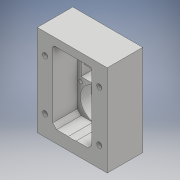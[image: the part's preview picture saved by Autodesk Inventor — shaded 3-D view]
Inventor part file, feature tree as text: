
AUTODESK INVENTOR PART (.ipt)
format: ipt  version: 2018 (Build 220112000, 112)  size: 443,392 bytes
history: native  units: mm
features: sketch x22, projected_geometry x19, extrude x18, hole x4, fillet x3, chamfer x1, mirror x1
ambient origin geometry x8: Origin, YZ Plane, XZ Plane, XY Plane, X Axis, Y Axis, Z Axis, Center Point
bodies: Solid1 (feature_tree)
feature tree (68):
  extrude  "Extrusion1"  Depth=45.0mm
  extrude  "Extrusion2"  Depth=1.95mm
  hole  "Hole1"  [1 undecoded]
  hole  "Hole2"  [1 undecoded]
  fillet  "Fillet1"  Radius=14.0mm
  extrude  "Extrusion3"  Depth=18.5mm
  extrude  "Extrusion4"  Depth=10.0mm
  extrude  "Extrusion5"  Depth=2.195mm
  extrude  "Extrusion6"  Depth=20.5mm
  hole  "Hole3"  [1 undecoded]
  extrude  "Extrusion7"  Depth=0.5mm
  extrude  "Extrusion8"  Depth=5.0mm TaperAngle=0.0deg
  extrude  "Extrusion9"  Depth=10.0mm
  extrude  "Extrusion10"  Depth=10.0mm
  extrude  "Extrusion11"  Depth=14.5mm
  extrude  "Extrusion12"  Depth=20.0mm
  extrude  "Extrusion13"  Depth=5.0mm
  extrude  "Extrusion14"  Depth=5.0mm
  extrude  "Extrusion15"  Depth=5.0mm
  extrude  "Extrusion16"  Depth=5.0mm
  extrude  "Extrusion17"  Depth=5.0mm
  chamfer  "Chamfer1"  Distance=1.0mm
  fillet  "Fillet7"  Radius=20.7mm
  fillet  "Fillet8"  Radius=32.0mm
  mirror  "Mirror1"
  extrude  "Extrusion18"  Depth=5.0mm TaperAngle=0.0deg
  hole  "Hole5"  [1 undecoded]
  sketch  "Sketch1"  dims[d0=24.5mm d1=45.0mm]
  sketch  "Sketch2"  dims[d2=1.95mm d3=0.0mm d4=2.25mm]
  projected_geometry  "Projected Loop1"
  sketch  "Sketch3"  dims[d5=20.0mm d6=2.25mm]
  projected_geometry  "Projected Loop2"
  sketch  "Sketch4"  dims[d7=5.25mm d8=5.25mm d9=14.0mm]
  projected_geometry  "Projected Loop3"
  sketch  "Sketch5"  dims[d10=5.25mm d11=18.5mm]
  projected_geometry  "Projected Loop4"
  sketch  "Sketch6"  dims[d12=10.0mm d13=0.0mm d14=20.5mm]
  projected_geometry  "Projected Loop5"
  sketch  "Sketch7"  dims[d15=2.0mm d16=2.195mm]
  projected_geometry  "Projected Loop6"
  sketch  "Sketch8"  dims[d17=2.0mm]
  projected_geometry  "Projected Loop7"
  sketch  "Sketch9"  dims[d18=2.4mm d19=6.0mm d20=4.4mm d21=2.0mm d22=90.0deg d23=8.0mm d24=20.594885mm d25=20.5mm]
  projected_geometry  "Projected Loop8"
  projected_geometry  "Projected Loop9"
  sketch  "Sketch10"  dims[d26=26.65mm d27=2.0mm]
  projected_geometry  "Projected Loop10"
  projected_geometry  "Projected Loop11"
  sketch  "Sketch11"  dims[d28=2.0mm]
  projected_geometry  "Projected Loop12"
  sketch  "Sketch12"  dims[d29=2.4mm d30=6.0mm d31=4.4mm d32=2.0mm d33=90.0deg d34=8.0mm d35=20.594885mm d36=0.5mm]
  sketch  "Sketch13"  dims[d37=18.0mm d38=5.0mm d39=0.0mm]
  sketch  "Sketch14"  dims[d41=10.0mm d42=0.0mm d43=24.5mm]
  projected_geometry  "Projected Loop13"
  sketch  "Sketch15"  dims[d44=1.15mm d45=0.0mm d46=10.0mm]
  sketch  "Sketch16"  dims[d47=21.0mm d48=14.5mm]
  projected_geometry  "Projected Loop14"
  sketch  "Sketch17"  dims[d49=20.0mm d50=14.5mm]
  projected_geometry  "Projected Loop15"
  sketch  "Sketch18"  dims[d51=24.5mm d52=5.0mm]
  projected_geometry  "Projected Loop16"
  sketch  "Sketch19"  dims[d53=5.0mm d54=2.25mm]
  projected_geometry  "Projected Loop17"
  sketch  "Sketch20"  dims[d55=2.25mm d56=5.0mm]
  projected_geometry  "Projected Loop18"
  sketch  "Sketch22"  dims[d57=5.0mm d58=9.0mm]
  sketch  "Sketch24"  dims[d59=14.75mm d60=4.0mm d61=1.0mm d62=0.0mm d63=20.7mm d64=2.4mm d65=6.0mm d66=4.4mm d67=2.0mm d68=90.0deg d69=8.0mm d70=20.594885mm d72=32.0mm d73=5.0mm d74=0.0mm d75=1.0mm d76=0.0mm d77=12.25mm d78=0.0mm d80=8.0mm d81=4.5mm d82=0.0mm d84=0.2mm d85=0.0mm d86=21.0mm d87=0.5mm d88=0.0mm d91=8.0mm d92=0.0mm d93=5.0mm d94=0.0mm d95=5.0mm d96=0.0mm d98=0.2mm d99=0.0mm d100=0.2mm d101=0.0mm d102=2.5mm d103=2.0mm d104=45.0deg d105=1.5mm d114=0.5mm d115=22.55mm d116=0.0mm d117=5.0mm d118=5.0mm d119=13.0mm d120=13.0mm d121=3.2mm d122=6.0mm d123=6.3mm d124=2.0mm d125=90.0deg d126=8.0mm d127=20.594885mm]
  projected_geometry  "Projected Loop21"
note: 4 required parameter values undecoded (feature->parameter linkage not recoverable at this tier; creation-order binding heuristic only, values carry confidence <= 0.55)
